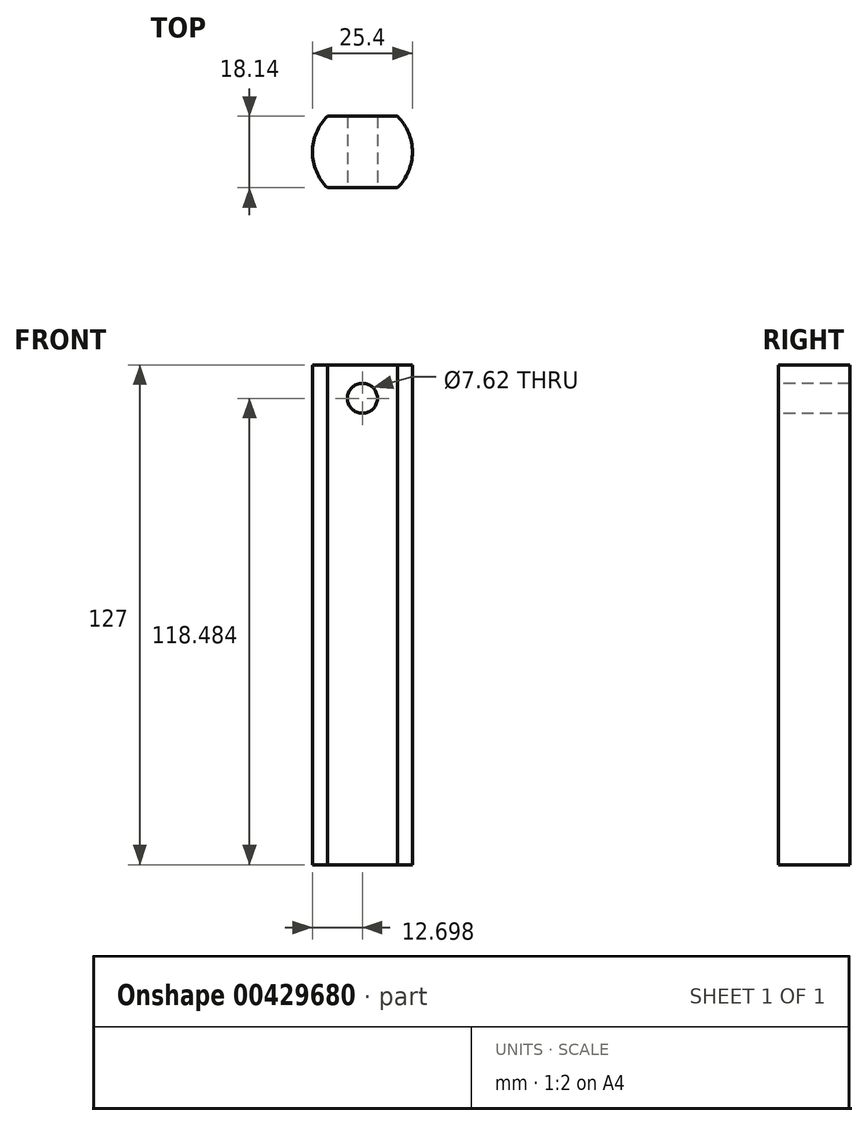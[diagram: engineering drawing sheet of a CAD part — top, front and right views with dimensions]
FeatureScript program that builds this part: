
annotation { "Feature Type Name" : "Feature", "Feature Type Description" : "" }
export const myFeature = defineFeature(function(context is Context, id is Id, definition is map)
    precondition{}
    {
        {
            var Q0;
            Q0=qCreatedBy(makeId("Top.planeOp"),FACE);
            var sketch = newSketch(context, id + "F0", { "sketchPlane" : qUnion([Q0])});
            skArc(sketch, "E0", {"start": v(-52.06, -34.78) * mm, "mid": v(-48.25, -25.71) * mm, "end": v(-52.06, -16.64) * mm});
            skLineSegment(sketch, "E1", {"start": v(-69.84, -34.78) * mm, "end": v(-52.06, -34.78) * mm});
            skLineSegment(sketch, "E2", {"start": v(-69.84, -16.64) * mm, "end": v(-52.06, -16.64) * mm});
            skArc(sketch, "E3.trimOffspring", {"start": v(-69.84, -16.64) * mm, "mid": v(-73.65, -25.71) * mm, "end": v(-69.84, -34.78) * mm});
            skSolve(sketch);
        }
        {
            var Q0;
            Q0 = qSketchRegion(id + "F0", true);
            extrude(context, id + "F1", {"entities" : qUnion([Q0]), "depth" : 127 * mm});
        }
        {
            var Q0;
            Q0=makeQuery(id+"F1.opExtrude","SWEPT_FACE",FACE,{"disambiguationData":[OSD([sQuery(id+"F0.wireOp",EDGE,"E1")])]});
            var sketch = newSketch(context, id + "F2", { "sketchPlane" : qUnion([Q0])});
            skCircle(sketch, "E4", {"center": v(-60.95, 118.48) * mm, "radius": 3.81 * mm});
            skPoint(sketch, "E4.centerSnap0", {"position": v(-60.95, 127) * mm});
            skSolve(sketch);
        }
        {
            var Q0;
            Q0 = qSketchRegion(id + "F2", true);
            extrude(context, id + "F3", {"entities" : qUnion([Q0]), "operationType" : NewBodyOperationType.REMOVE, "oppositeDirection" : true, "depth" : 25.4 * mm});
        }
    });
